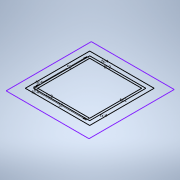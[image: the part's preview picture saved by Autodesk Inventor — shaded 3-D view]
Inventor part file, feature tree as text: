
AUTODESK INVENTOR PART (.ipt)
format: ipt  version: 2020.3 (Build 243373010, 373A)  size: 100,864 bytes
history: native  units: mm
features: sketch x1
ambient origin geometry x8: Origin, YZ Plane, XZ Plane, XY Plane, X Axis, Y Axis, Z Axis, Center Point
feature tree (1):
  sketch  "Sketch1"  dims[d0=50.0mm d1=50.0mm d2=2.0mm d3=2.0mm d4=2.0mm d5=2.0mm d6=4.0mm d7=4.0mm d8=4.0mm d9=4.0mm]
